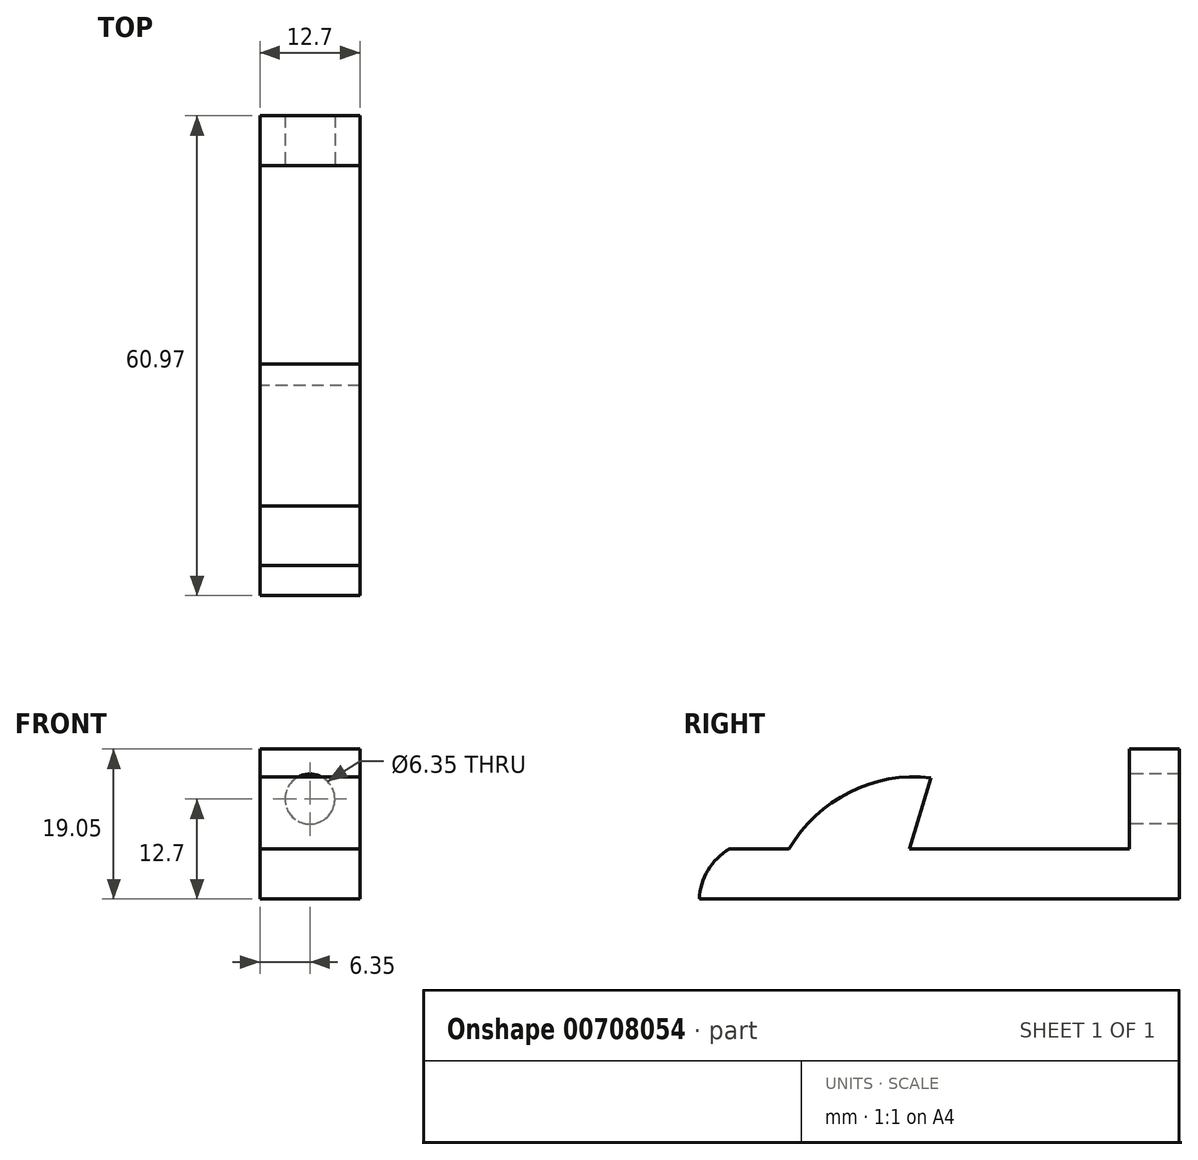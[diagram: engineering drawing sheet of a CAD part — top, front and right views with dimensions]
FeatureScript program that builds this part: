
annotation { "Feature Type Name" : "Feature", "Feature Type Description" : "" }
export const myFeature = defineFeature(function(context is Context, id is Id, definition is map)
    precondition{}
    {
        {
            var Q0;
            Q0=qCreatedBy(makeId("Right.planeOp"),FACE);
            var sketch = newSketch(context, id + "F0", { "sketchPlane" : qUnion([Q0])});
            skLineSegment(sketch, "E0.bottom", {"start": v(0, 0) * mm, "end": v(50.8, 0) * mm});
            skLineSegment(sketch, "E0.top", {"start": v(0, 6.35) * mm, "end": v(7.57, 6.35) * mm});
            skArc(sketch, "E1", {"start": v(25.59, 15.42) * mm, "mid": v(15.23, 13.57) * mm, "end": v(7.57, 6.35) * mm});
            skLineSegment(sketch, "E2", {"start": v(25.59, 15.42) * mm, "end": v(22.85, 6.35) * mm});
            skLineSegment(sketch, "E3.bottom", {"start": v(50.8, 0) * mm, "end": v(57.15, 0) * mm});
            skLineSegment(sketch, "E3.top", {"start": v(50.8, 19.05) * mm, "end": v(57.15, 19.05) * mm});
            skLineSegment(sketch, "E3.left", {"start": v(50.8, 6.35) * mm, "end": v(50.8, 19.05) * mm});
            skLineSegment(sketch, "E3.right", {"start": v(57.15, 0) * mm, "end": v(57.15, 19.05) * mm});
            skArc(sketch, "E4", {"start": v(0, 6.35) * mm, "mid": v(-2.73, 3.67) * mm, "end": v(-3.82, 0) * mm});
            skLineSegment(sketch, "E5", {"start": v(-3.82, 0) * mm, "end": v(0, 0) * mm});
            skLineSegment(sketch, "E6.trimOffspring", {"start": v(22.85, 6.35) * mm, "end": v(50.8, 6.35) * mm});
            skSolve(sketch);
        }
        {
            var Q0;
            Q0=makeQuery(id+"F0.imprint","IMPRINT",FACE,{"disambiguationData":[TD([[makeQuery(id+"F0.imprint","IMPRINT",EDGE,{"derivedFrom":sQuery(id+"F0.wireOp",EDGE,"E0.bottom")}),1.0]])]});
            extrude(context, id + "F1", {"entities" : qUnion([Q0]), "depth" : 12.7 * mm, "offsetDistance" : 25.4 * mm});
        }
        {
            var Q0;
            Q0=makeQuery(id+"F1.opExtrude","SWEPT_FACE",FACE,{"disambiguationData":[OSD([sQuery(id+"F0.wireOp",EDGE,"E3.left")])]});
            var sketch = newSketch(context, id + "F2", { "sketchPlane" : qUnion([Q0])});
            skLineSegment(sketch, "E7", {"start": v(0, 19.05) * mm, "end": v(12.7, 6.35) * mm, "construction": true});
            skLineSegment(sketch, "E8", {"start": v(0, 6.35) * mm, "end": v(12.7, 19.05) * mm, "construction": true});
            skCircle(sketch, "E9", {"center": v(6.35, 12.7) * mm, "radius": 3.18 * mm});
            skSolve(sketch);
        }
        {
            var Q0;
            Q0=makeQuery(id+"F2.imprint","IMPRINT",FACE,{"disambiguationData":[TD([[makeQuery(id+"F2.imprint","IMPRINT",EDGE,{"derivedFrom":sQuery(id+"F2.wireOp",EDGE,"E9")}),1.0]])]});
            extrude(context, id + "F3", {"entities" : qUnion([Q0]), "operationType" : NewBodyOperationType.REMOVE, "oppositeDirection" : true, "depth" : 25.4 * mm, "offsetDistance" : 25.4 * mm});
        }
    });
